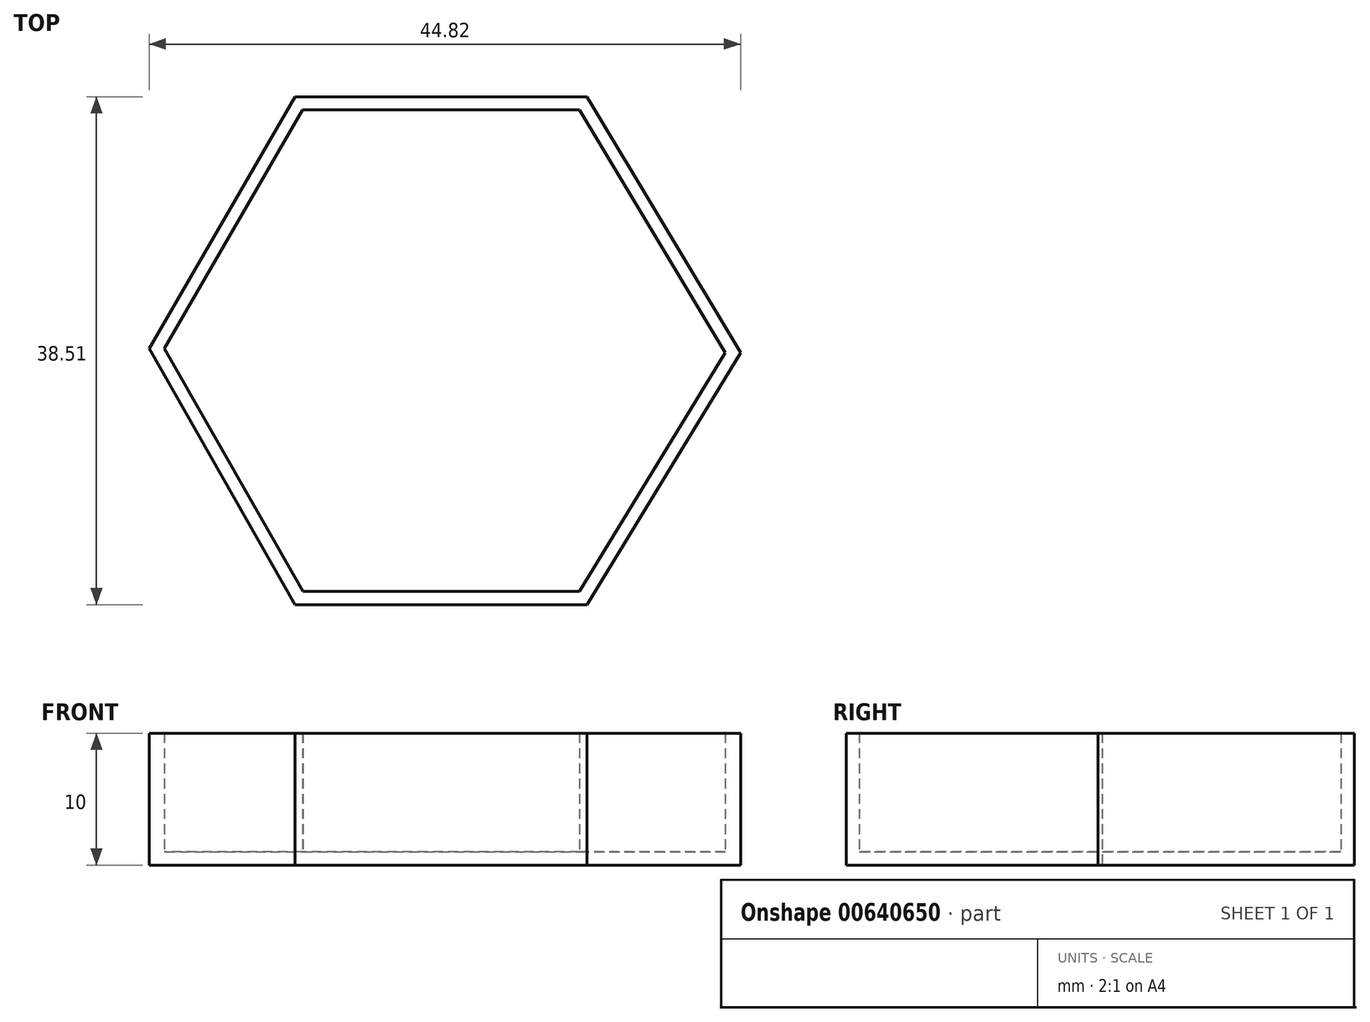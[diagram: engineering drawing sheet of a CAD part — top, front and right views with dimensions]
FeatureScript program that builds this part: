
annotation { "Feature Type Name" : "Feature", "Feature Type Description" : "" }
export const myFeature = defineFeature(function(context is Context, id is Id, definition is map)
    precondition{}
    {
        {
            var Q0;
            Q0=qCreatedBy(makeId("Top.planeOp"),FACE);
            var sketch = newSketch(context, id + "F0", { "sketchPlane" : qUnion([Q0])});
            skLineSegment(sketch, "E0", {"start": v(-23.3, 13.29) * mm, "end": v(-12.24, 32.4) * mm});
            skLineSegment(sketch, "E1", {"start": v(-12.24, 32.4) * mm, "end": v(9.87, 32.4) * mm});
            skLineSegment(sketch, "E2", {"start": v(9.87, 32.4) * mm, "end": v(21.52, 12.99) * mm});
            skLineSegment(sketch, "E3", {"start": v(21.52, 12.99) * mm, "end": v(9.87, -6.12) * mm});
            skLineSegment(sketch, "E4", {"start": v(9.87, -6.12) * mm, "end": v(-12.24, -6.12) * mm});
            skLineSegment(sketch, "E5", {"start": v(-12.24, -6.12) * mm, "end": v(-23.3, 13.29) * mm});
            skSolve(sketch);
        }
        {
            var Q0;
            Q0=makeQuery(id+"F0.imprint","IMPRINT",FACE,{"disambiguationData":[TD([[makeQuery(id+"F0.imprint","IMPRINT",EDGE,{"derivedFrom":sQuery(id+"F0.wireOp",EDGE,"E0")}),-1.0]])]});
            extrude(context, id + "F1", {"entities" : qUnion([Q0]), "depth" : 10 * mm, "offsetDistance" : 25.4 * mm});
        }
        {
            var Q0;
            Q0=makeQuery(id+"F1.opExtrude","CAP_FACE",FACE,{"disambiguationData":[OSD([sQuery(id+"F0.wireOp",EDGE,"E0"),sQuery(id+"F0.wireOp",EDGE,"E1"),sQuery(id+"F0.wireOp",EDGE,"E2"),sQuery(id+"F0.wireOp",EDGE,"E3"),sQuery(id+"F0.wireOp",EDGE,"E4"),sQuery(id+"F0.wireOp",EDGE,"E5")])],"isStart":false});
            shell(context, id + "F2", {"entities" : qUnion([Q0]), "thickness" : 1 * mm});
        }
    });
